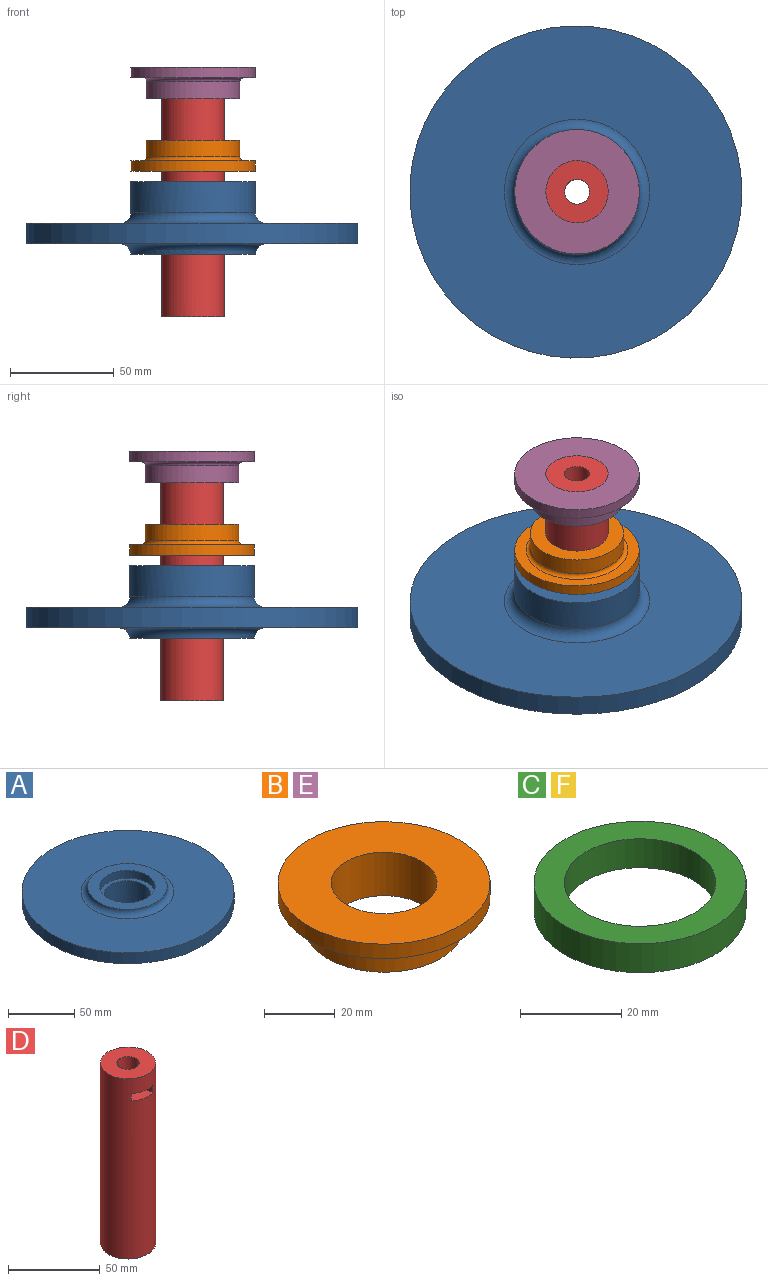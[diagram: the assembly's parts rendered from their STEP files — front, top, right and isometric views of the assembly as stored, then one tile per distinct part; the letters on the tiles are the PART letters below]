
ASSEMBLY  parts=6 mates=5
PART A: 13 faces, bbox 160x160x38.6 mm
  f0: cylinder r=80mm len=160mm, axis (0,0,-1), area 5026.5mm2, adj f8,f10
  f1: cylinder r=17.5mm len=35mm, axis (0,0,-1), area 2309.1mm2, adj f4,f7
  f2: plane 60x60mm, normal (0,0,-1), area 1442mm2, adj f3,f9
  f3: cylinder r=21mm len=42mm, axis (0,0,-1), area 923.6mm2, adj f2,f4
  f4: plane 42x42mm, normal (0,0,-1), area 423.3mm2, adj f1,f3
  f5: plane 60x60mm, normal (0,0,1), area 1442mm2, adj f6,f11
  f6: cylinder r=21mm len=42mm, axis (0,0,1), area 923.6mm2, adj f5,f7
  f7: plane 42x42mm, normal (0,0,1), area 423.3mm2, adj f1,f6
  f8: plane 160x160mm, normal (0,0,1), area 16257.7mm2, adj f0,f11
  f9: cylinder r=30mm len=60mm, axis (0,0,-1), area 2827.4mm2, adj f2,f12
  f10: plane 160x160mm, normal (0,0,-1), area 16257.7mm2, adj f0,f12
  f11: torus R=35mm, axis (0,0,-1), area 1570.1mm2, adj f5,f8
  f12: torus R=35mm, axis (0,0,-1), area 1570.1mm2, adj f9,f10
PART B: 7 faces, bbox 60x60x15 mm
  f0: cylinder r=22.5mm len=45mm, axis (0,0,-1), area 1131mm2, adj f3,f6
  f1: cylinder r=15mm len=30mm, axis (0,0,-1), area 1413.7mm2, adj f2,f3
  f2: plane 60x60mm, normal (0,0,1), area 2120.6mm2, adj f1,f4
  f3: plane 45x45mm, normal (0,0,-1), area 883.6mm2, adj f0,f1
  f4: cylinder r=30mm len=60mm, axis (0,0,1), area 942.5mm2, adj f2,f5
  f5: plane 60x60mm, normal (0,0,-1), area 941.7mm2, adj f4,f6
  f6: torus R=24.5mm, axis (0,0,1), area 458.5mm2, adj f0,f5
PART C: 4 faces, bbox 42x42x7 mm
  f0: cylinder r=15mm len=30mm, axis (0,0,-1), area 659.7mm2, adj f2,f3
  f1: cylinder r=21mm len=42mm, axis (0,0,-1), area 923.6mm2, adj f2,f3
  f2: plane 42x42mm, normal (0,0,1), area 678.6mm2, adj f0,f1
  f3: plane 42x42mm, normal (0,0,-1), area 678.6mm2, adj f0,f1
PART D: 10 faces, bbox 30x30x120 mm
  f0: plane 21x21mm, normal (0,0,-1), area 233.3mm2, adj f1,f8
  f1: cylinder r=6mm len=90mm, axis (0,0,-1), area 3345.3mm2, adj f0,f2,f4,f5,f6,f7
  f2: plane 30x30mm, normal (0,0,1), area 593.8mm2, adj f1,f3
  f3: cylinder r=15mm len=120mm, axis (0,0,-1), area 11235.4mm2, adj f2,f4,f5,f6,f7,f9
  f4: plane 8.32x5mm, normal (0.89,-0.46,0), area 47mm2, adj f1,f3,f6,f7
  f5: plane 9.39x5mm, normal (-0.99,-0.13,0), area 47.4mm2, adj f1,f3,f6,f7
  f6: plane 14.07x11.49mm, normal (0,0,1), area 109.4mm2, adj f1,f3,f4,f5
  f7: plane 14.07x11.49mm, normal (0,0,-1), area 109.4mm2, adj f1,f3,f4,f5
  f8: cylinder r=10.5mm len=30mm, axis (0,0,1), area 1979.2mm2, adj f0,f9
  f9: plane 30x30mm, normal (0,0,-1), area 360.5mm2, adj f3,f8
PART E: same geometry as B
PART F: same geometry as C
PLACE A rot(axis=(0,1,0),180deg) t=(170.84,-3.37,131.65)mm
PLACE B rot(axis=(1,0,0),180deg) t=(170.84,-3.37,161.65)mm
PLACE C t=(170.84,-3.37,138.15)mm
PLACE D t=(170.84,-3.37,106.65)mm
PLACE E t=(170.84,-3.37,181.65)mm
PLACE F t=(170.84,-3.37,110.15)mm
MATE revolute F.f0 <-> A.f1  axis (0,0,1) through (170.84,-3.37,113.65)mm
MATE revolute A.f1 <-> C.f1  axis (0,0,1) through (170.84,-3.37,134.65)mm
MATE fastened C.f0 <-> E.f4  axis (0,0,1) through (170.84,-3.37,141.65)mm
MATE fastened B.f1 <-> E.f4  axis (0,0,-1) through (170.84,-3.37,146.65)mm
MATE fastened E.f4 <-> D.f1  axis (0,0,1) through (170.84,-3.37,196.65)mm
